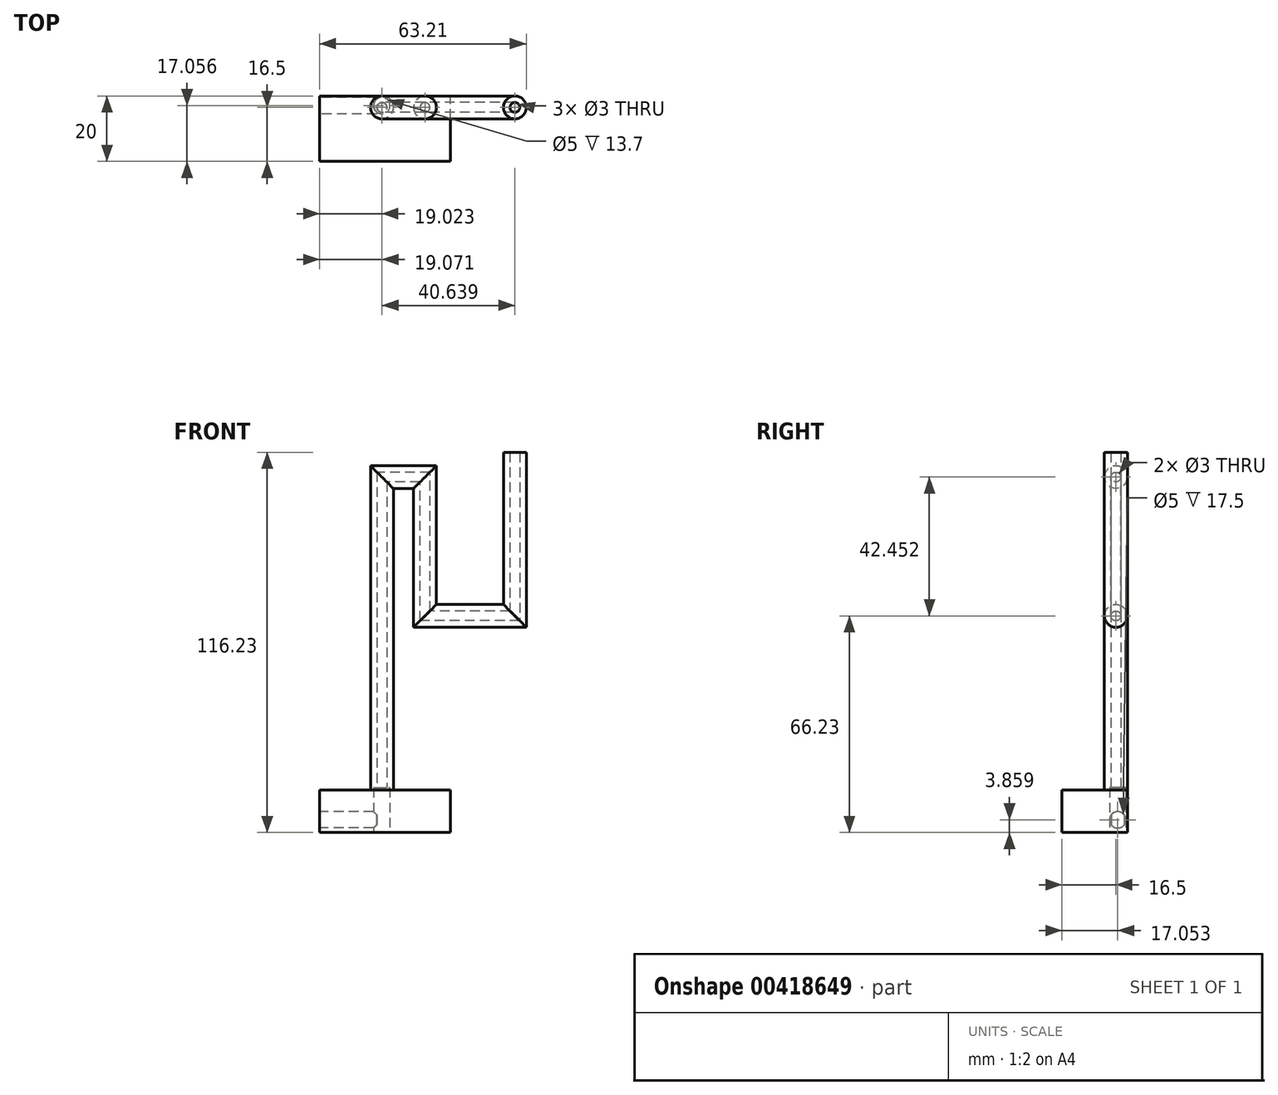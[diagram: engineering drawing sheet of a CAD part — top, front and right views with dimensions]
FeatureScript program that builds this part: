
annotation { "Feature Type Name" : "Feature", "Feature Type Description" : "" }
export const myFeature = defineFeature(function(context is Context, id is Id, definition is map)
    precondition{}
    {
        {
            var Q0;
            Q0=qCreatedBy(makeId("Front.planeOp"),FACE);
            var sketch = newSketch(context, id + "F0", { "sketchPlane" : qUnion([Q0])});
            skLineSegment(sketch, "E0.bottom", {"start": v(-200, 0) * mm, "end": v(0, 0) * mm});
            skLineSegment(sketch, "E0.top", {"start": v(-200, -120) * mm, "end": v(0, -120) * mm});
            skLineSegment(sketch, "E0.left", {"start": v(-200, 0) * mm, "end": v(-200, -120) * mm});
            skLineSegment(sketch, "E0.right", {"start": v(0, 0) * mm, "end": v(0, -120) * mm});
            skSolve(sketch);
        }
        {
            var Q0;
            Q0=qCreatedBy(makeId("Top.planeOp"),FACE);
            var sketch = newSketch(context, id + "F1", { "sketchPlane" : qUnion([Q0])});
            skCircle(sketch, "E1", {"center": v(-5.28, -3.5) * mm, "radius": 3.5 * mm});
            skCircle(sketch, "E2", {"center": v(-5.28, -3.5) * mm, "radius": 1.5 * mm});
            skSolve(sketch);
        }
        {
            var Q0;
            Q0=makeQuery(id+"F0.imprint","IMPRINT",FACE,{"disambiguationData":[TD([[makeQuery(id+"F0.imprint","IMPRINT",EDGE,{"derivedFrom":sQuery(id+"F0.wireOp",EDGE,"E0.bottom")}),-1.0]])]});
            var sketch = newSketch(context, id + "F2", { "sketchPlane" : qUnion([Q0])});
            skLineSegment(sketch, "E3", {"start": v(-5.28, 0) * mm, "end": v(-5.28, -50) * mm});
            skLineSegment(sketch, "E4", {"start": v(-5.28, -50) * mm, "end": v(-32.75, -50) * mm});
            skLineSegment(sketch, "E5", {"start": v(-32.75, -50) * mm, "end": v(-32.75, -7.55) * mm});
            skLineSegment(sketch, "E6", {"start": v(-32.75, -7.55) * mm, "end": v(-45.92, -7.55) * mm});
            skLineSegment(sketch, "E7", {"start": v(-45.92, -7.55) * mm, "end": v(-45.92, -111.43) * mm});
            skSolve(sketch);
        }
        {
            var Q0;
            Q0=makeQuery(id+"F1.imprint","IMPRINT",FACE,{"disambiguationData":[TD([[makeQuery(id+"F1.imprint","IMPRINT",EDGE,{"derivedFrom":sQuery(id+"F1.wireOp",EDGE,"E1")}),1.0]])]});
            var Q1;
            Q1=sQuery(id+"F2.wireOp",EDGE,"E3");
            var Q2;
            Q2=sQuery(id+"F2.wireOp",EDGE,"E4");
            var Q3;
            Q3=sQuery(id+"F2.wireOp",EDGE,"E5");
            var Q4;
            Q4=sQuery(id+"F2.wireOp",EDGE,"E6");
            var Q5;
            Q5=sQuery(id+"F2.wireOp",EDGE,"E7");
            sweep(context, id + "F3", {"profiles" : qUnion([Q0]), "path" : qUnion([Q1, Q2, Q3, Q4, Q5])});
        }
        {
            var Q0;
            Q0=makeQuery(id+"F0.imprint","IMPRINT",FACE,{"disambiguationData":[TD([[makeQuery(id+"F0.imprint","IMPRINT",EDGE,{"derivedFrom":sQuery(id+"F0.wireOp",EDGE,"E0.bottom")}),-1.0]])]});
            var sketch = newSketch(context, id + "F4", { "sketchPlane" : qUnion([Q0])});
            skLineSegment(sketch, "E8.bottom", {"start": v(-64.99, -103.23) * mm, "end": v(-24.99, -103.23) * mm});
            skLineSegment(sketch, "E8.top", {"start": v(-64.99, -116.23) * mm, "end": v(-24.99, -116.23) * mm});
            skLineSegment(sketch, "E8.left", {"start": v(-64.99, -103.23) * mm, "end": v(-64.99, -116.23) * mm});
            skLineSegment(sketch, "E8.right", {"start": v(-24.99, -103.23) * mm, "end": v(-24.99, -116.23) * mm});
            skSolve(sketch);
        }
        {
            var Q0;
            Q0 = qSketchRegion(id + "F4", true);
            var Q1;
            Q1=sQuery(id+"F4.wireOp",EDGE,"E8.top");
            var Q2;
            Q2=sQuery(id+"F4.wireOp",EDGE,"E8.right");
            var Q3;
            Q3=sQuery(id+"F4.wireOp",EDGE,"E8.bottom");
            var Q4;
            Q4=sQuery(id+"F4.wireOp",EDGE,"E8.left");
            extrude(context, id + "F5", {"entities" : qUnion([Q0]), "operationType" : NewBodyOperationType.ADD, "surfaceEntities" : qUnion([Q1, Q2, Q3, Q4]), "depth" : 20 * mm});
        }
        {
            var Q0;
            Q0=makeQuery(id+"F5.opExtrude","SWEPT_FACE",FACE,{"disambiguationData":[OSD([sQuery(id+"F4.wireOp",EDGE,"E8.left")])]});
            var sketch = newSketch(context, id + "F6", { "sketchPlane" : qUnion([Q0])});
            skCircle(sketch, "E9", {"center": v(2.95, -112.37) * mm, "radius": 2.5 * mm});
            skSolve(sketch);
        }
        {
            var Q0;
            Q0 = qSketchRegion(id + "F6", true);
            extrude(context, id + "F7", {"entities" : qUnion([Q0]), "operationType" : NewBodyOperationType.REMOVE, "oppositeDirection" : true, "depth" : 17.5 * mm});
        }
        {
            var Q0;
            Q0=makeQuery(id+"F5.opExtrude","SWEPT_FACE",FACE,{"disambiguationData":[OSD([sQuery(id+"F4.wireOp",EDGE,"E8.top")])]});
            var sketch = newSketch(context, id + "F8", { "sketchPlane" : qUnion([Q0])});
            skCircle(sketch, "E10", {"center": v(-45.97, 2.94) * mm, "radius": 2.5 * mm});
            skSolve(sketch);
        }
        {
            var Q0;
            Q0 = qSketchRegion(id + "F8", true);
            extrude(context, id + "F9", {"entities" : qUnion([Q0]), "operationType" : NewBodyOperationType.REMOVE, "oppositeDirection" : true, "depth" : 13.7 * mm});
        }
    });
